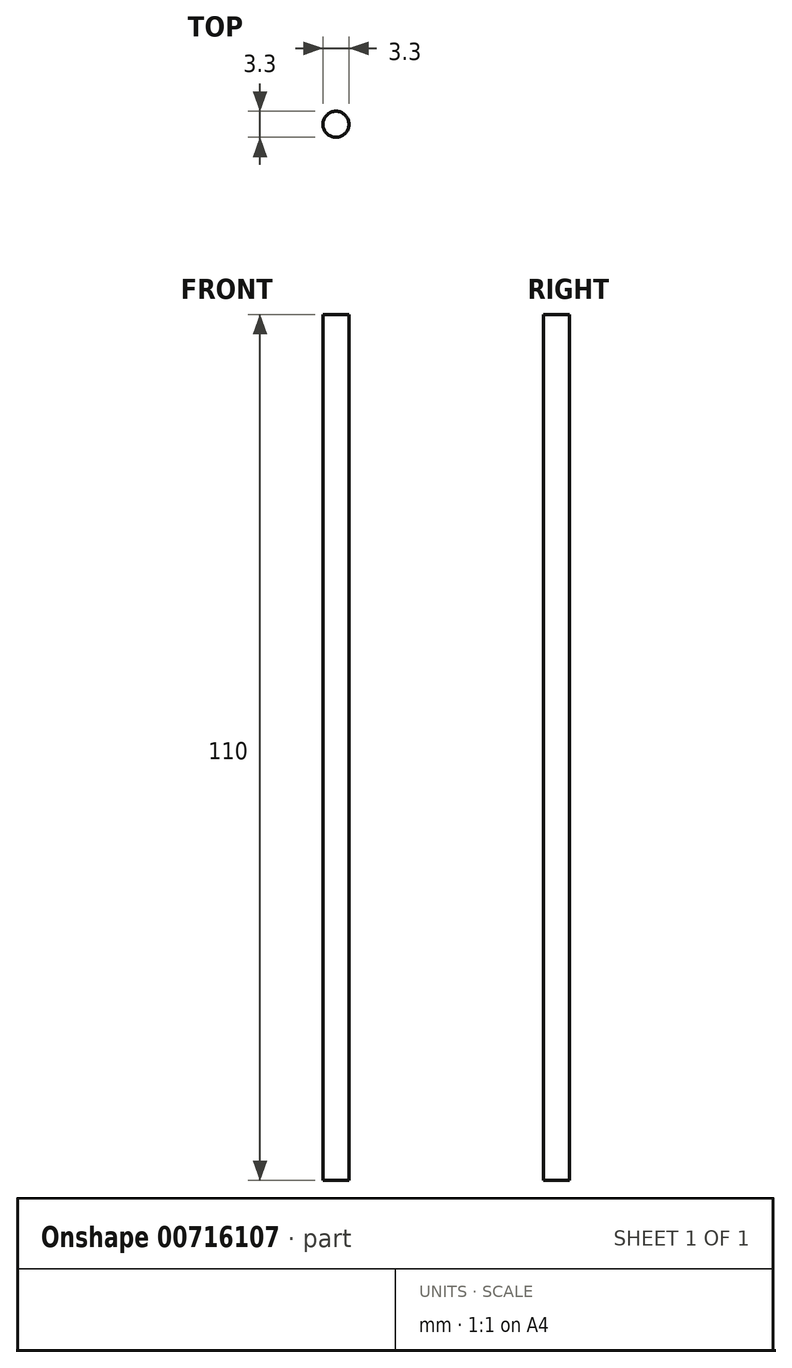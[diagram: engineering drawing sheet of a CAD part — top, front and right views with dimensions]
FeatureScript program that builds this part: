
annotation { "Feature Type Name" : "Feature", "Feature Type Description" : "" }
export const myFeature = defineFeature(function(context is Context, id is Id, definition is map)
    precondition{}
    {
        {
            var Q0;
            Q0=qCreatedBy(makeId("Top.planeOp"),FACE);
            var sketch = newSketch(context, id + "F0", { "sketchPlane" : qUnion([Q0])});
            skCircle(sketch, "E0", {"center": v(0, 0) * mm, "radius": 1.65 * mm});
            skSolve(sketch);
        }
        {
            var Q0;
            Q0=makeQuery(id+"F0.imprint","IMPRINT",FACE,{"disambiguationData":[TD([[makeQuery(id+"F0.imprint","IMPRINT",EDGE,{"derivedFrom":sQuery(id+"F0.wireOp",EDGE,"E0")}),1.0]])]});
            extrude(context, id + "F1", {"entities" : qUnion([Q0]), "endBound" : BoundingType.SYMMETRIC, "depth" : 110 * mm, "offsetDistance" : 25 * mm});
        }
    });
